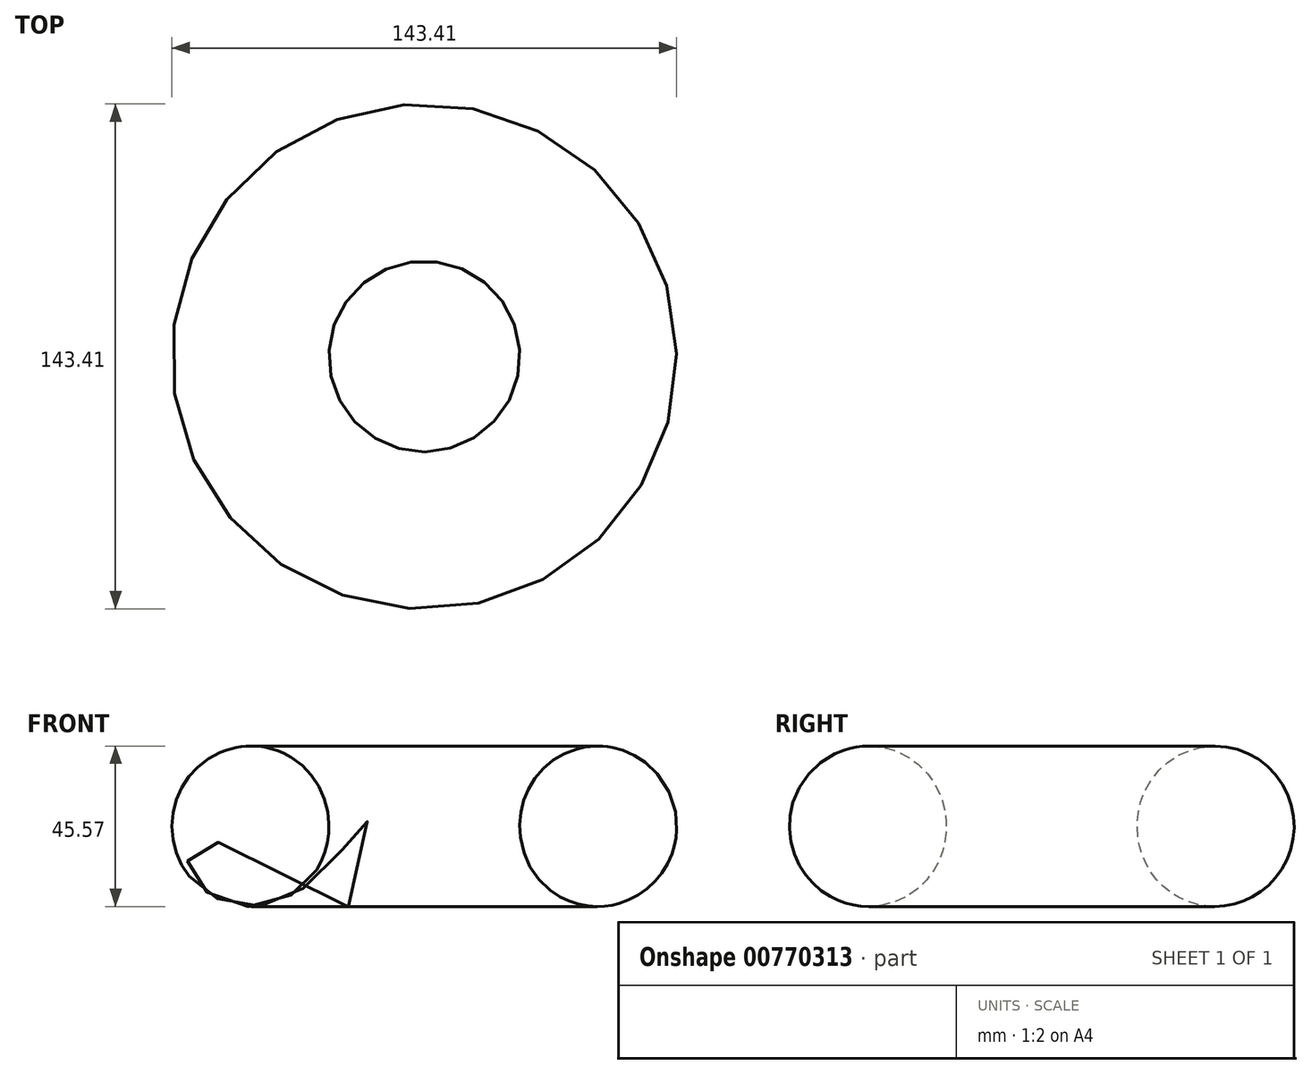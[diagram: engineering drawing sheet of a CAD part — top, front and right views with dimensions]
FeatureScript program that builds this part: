
annotation { "Feature Type Name" : "Feature", "Feature Type Description" : "" }
export const myFeature = defineFeature(function(context is Context, id is Id, definition is map)
    precondition{}
    {
        {
            var Q0;
            Q0=qCreatedBy(makeId("Front.planeOp"),FACE);
            var sketch = newSketch(context, id + "F0", { "sketchPlane" : qUnion([Q0])});
            skPoint(sketch, "E0", {"position": v(35.7, 34.14) * mm});
            skCircle(sketch, "E1", {"center": v(35.7, 34.14) * mm, "radius": 22.78 * mm});
            skPoint(sketch, "E2", {"position": v(35.7, 11.36) * mm});
            skSolve(sketch);
        }
        {
            var Q0;
            Q0=qCreatedBy(makeId("Top.planeOp"),FACE);
            cPlane(context, id + "F1", {"entities" : qUnion([Q0]), "cplaneType" : CPlaneType.OFFSET, "offset" : 34.14 * mm, "width" : 150 * mm, "height" : 150 * mm});
        }
        {
            var Q0;
            Q0=qCreatedBy(id+"F1.planeOp",FACE);
            var sketch = newSketch(context, id + "F2", { "sketchPlane" : qUnion([Q0])});
            skCircle(sketch, "E3", {"center": v(-12.66, 9) * mm, "radius": 49.2 * mm});
            skPoint(sketch, "E3.first.point", {"position": v(35.7, 0) * mm});
            skPoint(sketch, "E3.second.point", {"position": v(-31.87, 54.28) * mm});
            skPoint(sketch, "E3.third.point", {"position": v(-51.78, -20.83) * mm});
            skSolve(sketch);
        }
        {
            var Q0;
            Q0=makeQuery(id+"F0.imprint","IMPRINT",FACE,{"disambiguationData":[TD([[makeQuery(id+"F0.imprint","IMPRINT",EDGE,{"derivedFrom":sQuery(id+"F0.wireOp",EDGE,"E1")}),1.0]])]});
            var Q1;
            Q1=sQuery(id+"F2.wireOp",EDGE,"E3");
            sweep(context, id + "F3", {"profiles" : qUnion([Q0]), "path" : qUnion([Q1])});
        }
    });
